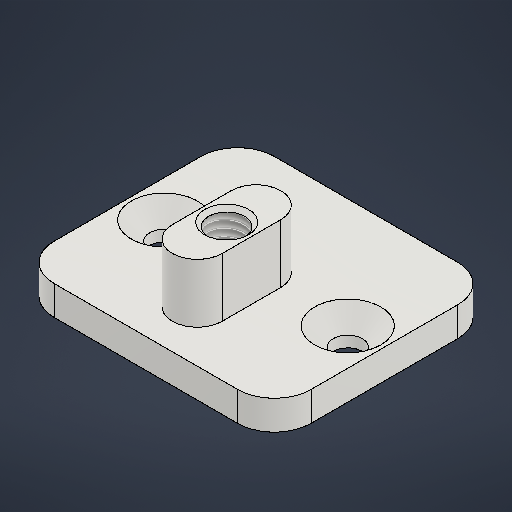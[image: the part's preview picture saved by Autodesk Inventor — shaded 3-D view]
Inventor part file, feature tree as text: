
AUTODESK INVENTOR PART (.ipt)
format: ipt  version: 2025.3 (Build 293356000, 356)  size: 218,112 bytes
history: native  units: mm
features: sketch x2, extrude x2, hole x2, fillet x1
ambient origin geometry x8: Origin, YZ Plane, XZ Plane, XY Plane, X Axis, Y Axis, Z Axis, Center Point
bodies: Solid1 (feature_tree)
feature tree (7):
  sketch  "Sketch1"  dims[d0=35.0mm d1=30.0mm]
  extrude  "Extrusion1"  Depth=30.0mm
  extrude  "Extrusion2"  Depth=8.0mm
  hole  "Hole1"  [1 undecoded]
  hole  "Hole2"  [1 undecoded]
  fillet  "Fillet1"  Radius=12.0mm
  sketch  "Sketch2"  dims[d2=6.8mm d3=8.0mm d4=0.0mm d5=25.0mm d6=12.0mm d7=0.0mm d8=8.0mm d9=0.0mm d10=4.917mm d11=12.0mm d12=6.0mm d13=2.0mm d14=90.0deg d15=8.0mm d16=20.594885mm d17=4.0mm d18=12.0mm d19=9.0mm d20=2.0mm d21=90.0deg d22=8.0mm d23=20.594885mm d24=5.0mm]
note: 2 required parameter values undecoded (feature->parameter linkage not recoverable at this tier; creation-order binding heuristic only, values carry confidence <= 0.55)
